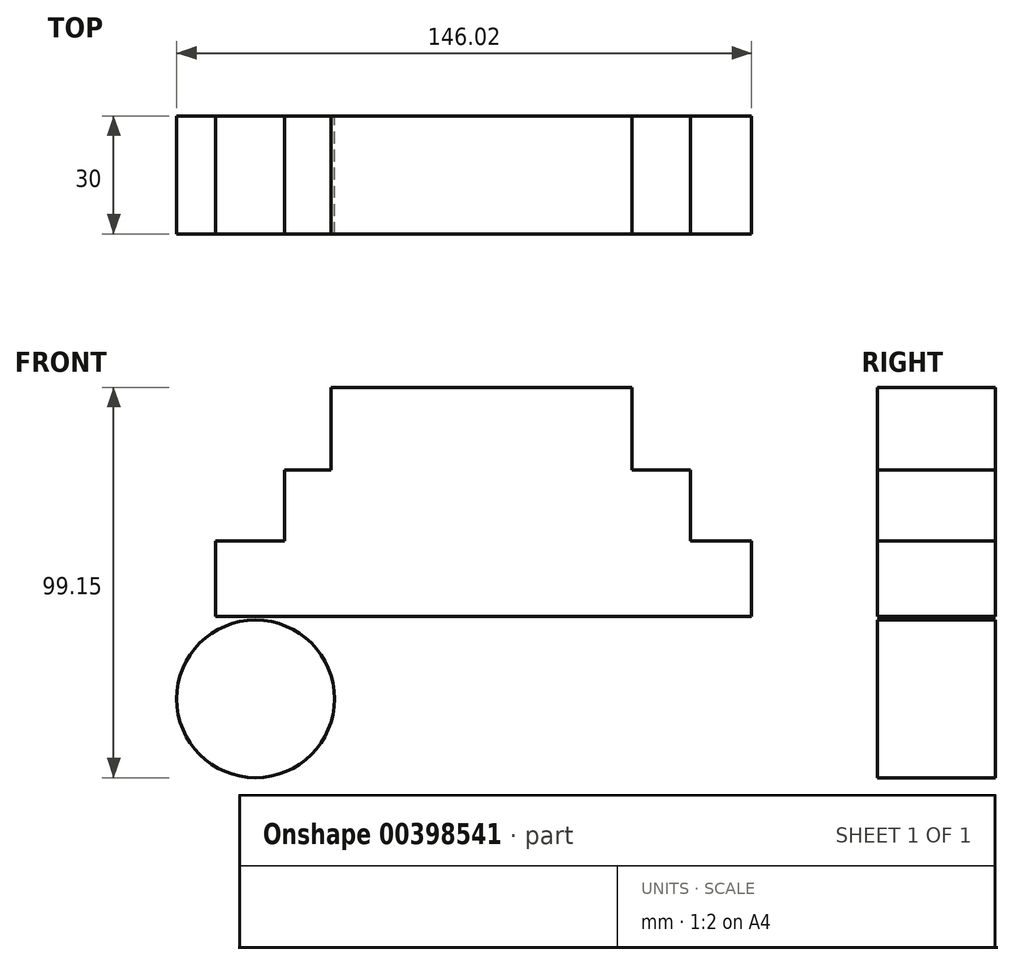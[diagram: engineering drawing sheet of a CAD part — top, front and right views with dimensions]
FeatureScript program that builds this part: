
annotation { "Feature Type Name" : "Feature", "Feature Type Description" : "" }
export const myFeature = defineFeature(function(context is Context, id is Id, definition is map)
    precondition{}
    {
        {
            var Q0;
            Q0=qCreatedBy(makeId("Front.planeOp"),FACE);
            var sketch = newSketch(context, id + "F0", { "sketchPlane" : qUnion([Q0])});
            skLineSegment(sketch, "E0.bottom", {"start": v(-36.83, 26.63) * mm, "end": v(39.66, 26.63) * mm});
            skLineSegment(sketch, "E0.top", {"start": v(-36.83, 5.67) * mm, "end": v(39.66, 5.67) * mm});
            skLineSegment(sketch, "E0.left", {"start": v(-36.83, 26.63) * mm, "end": v(-36.83, 5.67) * mm});
            skLineSegment(sketch, "E0.right", {"start": v(39.66, 26.63) * mm, "end": v(39.66, 5.67) * mm});
            skLineSegment(sketch, "E1.bottom", {"start": v(31.16, 26.63) * mm, "end": v(-28.9, 26.63) * mm});
            skLineSegment(sketch, "E1.top", {"start": v(31.16, 43.9) * mm, "end": v(-28.9, 43.9) * mm});
            skLineSegment(sketch, "E1.left", {"start": v(31.16, 26.63) * mm, "end": v(31.16, 43.9) * mm});
            skLineSegment(sketch, "E1.right", {"start": v(-28.9, 26.63) * mm, "end": v(-28.9, 43.9) * mm});
            skLineSegment(sketch, "E2.bottom", {"start": v(21.81, 43.9) * mm, "end": v(-20.4, 43.9) * mm});
            skLineSegment(sketch, "E2.top", {"start": v(21.81, 56.09) * mm, "end": v(-20.4, 56.09) * mm});
            skLineSegment(sketch, "E2.left", {"start": v(21.81, 43.9) * mm, "end": v(21.81, 56.09) * mm});
            skLineSegment(sketch, "E2.right", {"start": v(-20.4, 43.9) * mm, "end": v(-20.4, 56.09) * mm});
            skLineSegment(sketch, "E3.bottom", {"start": v(14.73, 56.09) * mm, "end": v(-13.03, 56.09) * mm});
            skLineSegment(sketch, "E3.top", {"start": v(14.73, 63.45) * mm, "end": v(-13.03, 63.45) * mm});
            skLineSegment(sketch, "E3.left", {"start": v(14.73, 56.09) * mm, "end": v(14.73, 63.45) * mm});
            skLineSegment(sketch, "E3.right", {"start": v(-13.03, 56.09) * mm, "end": v(-13.03, 63.45) * mm});
            skLineSegment(sketch, "E4.bottom", {"start": v(8.21, 63.45) * mm, "end": v(-6.23, 63.45) * mm});
            skLineSegment(sketch, "E4.top", {"start": v(8.21, 68.84) * mm, "end": v(-6.23, 68.84) * mm});
            skLineSegment(sketch, "E4.left", {"start": v(8.21, 63.45) * mm, "end": v(8.21, 68.84) * mm});
            skLineSegment(sketch, "E4.right", {"start": v(-6.23, 63.45) * mm, "end": v(-6.23, 68.84) * mm});
            skLineSegment(sketch, "E5.bottom", {"start": v(-48.59, 5.67) * mm, "end": v(54.5, 5.67) * mm});
            skLineSegment(sketch, "E5.top", {"start": v(-48.59, -12.4) * mm, "end": v(54.5, -12.4) * mm});
            skLineSegment(sketch, "E5.left", {"start": v(-48.59, 5.67) * mm, "end": v(-48.59, -12.4) * mm});
            skLineSegment(sketch, "E5.right", {"start": v(54.5, 5.67) * mm, "end": v(54.5, -12.4) * mm});
            skLineSegment(sketch, "E6.bottom", {"start": v(70, -12.4) * mm, "end": v(-66.1, -12.4) * mm});
            skLineSegment(sketch, "E6.top", {"start": v(70, -31.6) * mm, "end": v(-66.1, -31.6) * mm});
            skLineSegment(sketch, "E6.left", {"start": v(70, -12.4) * mm, "end": v(70, -31.6) * mm});
            skLineSegment(sketch, "E6.right", {"start": v(-66.1, -12.4) * mm, "end": v(-66.1, -31.6) * mm});
            skCircle(sketch, "E7", {"center": v(-56, -52.5) * mm, "radius": 20.03 * mm});
            skCircle(sketch, "E8.MirrorC", {"center": v(56, -52.5) * mm, "radius": 20.03 * mm});
            skSolve(sketch);
        }
        {
            var Q0;
            Q0=makeQuery(id+"F0.imprint","IMPRINT",FACE,{"disambiguationData":[TD([[makeQuery(id+"F0.imprint","IMPRINT",EDGE,{"derivedFrom":sQuery(id+"F0.wireOp",EDGE,"E7")}),1.0]])]});
            var Q1;
            Q1=makeQuery(id+"F0.imprint","IMPRINT",FACE,{"disambiguationData":[TD([[makeQuery(id+"F0.imprint","IMPRINT",EDGE,{"derivedFrom":sQuery(id+"F0.wireOp",EDGE,"E8.MirrorC")}),-1.0]])]});
            var Q2;
            Q2=makeQuery(id+"F0.imprint","IMPRINT",FACE,{"disambiguationData":[TD([[makeQuery(id+"F0.imprint","IMPRINT",EDGE,{"derivedFrom":sQuery(id+"F0.wireOp",EDGE,"E4.bottom")}),-1.0]])]});
            var Q3;
            {var subQ1=sQuery(id+"F0.wireOp",EDGE,"E0.left");Q3=makeQuery(id+"F0.imprint","IMPRINT",FACE,{"disambiguationData":[TD([[makeQuery(id+"F0.imprint","IMPRINT",EDGE,{"derivedFrom":subQ1}),1.0]])]});}
            var Q4;
            Q4=makeQuery(id+"F0.imprint","IMPRINT",FACE,{"disambiguationData":[TD([[makeQuery(id+"F0.imprint","IMPRINT",EDGE,{"derivedFrom":sQuery(id+"F0.wireOp",EDGE,"E1.bottom")}),-1.0]])]});
            var Q5;
            Q5=makeQuery(id+"F0.imprint","IMPRINT",FACE,{"disambiguationData":[TD([[makeQuery(id+"F0.imprint","IMPRINT",EDGE,{"derivedFrom":sQuery(id+"F0.wireOp",EDGE,"E2.bottom")}),-1.0]])]});
            var Q6;
            Q6=makeQuery(id+"F0.imprint","IMPRINT",FACE,{"disambiguationData":[TD([[makeQuery(id+"F0.imprint","IMPRINT",EDGE,{"derivedFrom":sQuery(id+"F0.wireOp",EDGE,"E3.bottom")}),-1.0]])]});
            var Q7;
            {var subQ0=sQuery(id+"F0.wireOp",EDGE,"E5.left");Q7=makeQuery(id+"F0.imprint","IMPRINT",FACE,{"disambiguationData":[TD([[makeQuery(id+"F0.imprint","IMPRINT",EDGE,{"derivedFrom":subQ0}),1.0]])]});}
            var Q8;
            Q8=makeQuery(id+"F0.imprint","IMPRINT",FACE,{"disambiguationData":[TD([[makeQuery(id+"F0.imprint","IMPRINT",EDGE,{"derivedFrom":sQuery(id+"F0.wireOp",EDGE,"E6.top")}),-1.0]])]});
            extrude(context, id + "F1", {"entities" : qUnion([Q0, Q1, Q2, Q3, Q4, Q5, Q6, Q7, Q8]), "depth" : 30 * mm});
        }
    });
